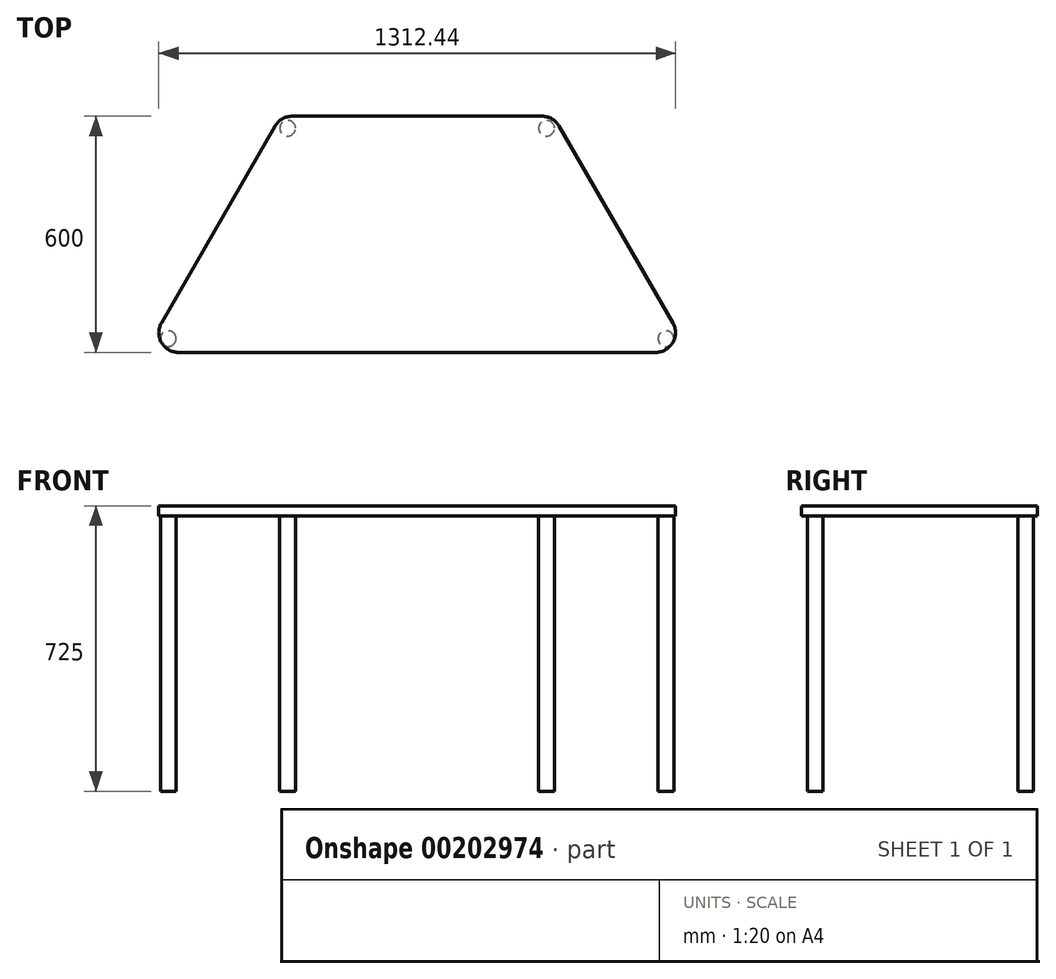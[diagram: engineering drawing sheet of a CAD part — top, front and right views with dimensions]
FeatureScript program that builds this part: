
annotation { "Feature Type Name" : "Feature", "Feature Type Description" : "" }
export const myFeature = defineFeature(function(context is Context, id is Id, definition is map)
    precondition{}
    {
        {
            var Q0;
            Q0=qCreatedBy(makeId("Top.planeOp"),FACE);
            var sketch = newSketch(context, id + "F0", { "sketchPlane" : qUnion([Q0])});
            skLineSegment(sketch, "E0", {"start": v(0, 300) * mm, "end": v(-346.41, 300) * mm});
            skLineSegment(sketch, "E1", {"start": v(-346.41, 300) * mm, "end": v(-692.82, -300) * mm});
            skLineSegment(sketch, "E2", {"start": v(-692.82, -300) * mm, "end": v(0, -300) * mm});
            skLineSegment(sketch, "E3.MirrorCS", {"start": v(0, 300) * mm, "end": v(346.41, 300) * mm});
            skLineSegment(sketch, "E4.MirrorCS", {"start": v(346.41, 300) * mm, "end": v(692.82, -300) * mm});
            skLineSegment(sketch, "E5.MirrorCS", {"start": v(692.82, -300) * mm, "end": v(0, -300) * mm});
            skLineSegment(sketch, "E6", {"start": v(0, 300) * mm, "end": v(0, 0) * mm});
            skLineSegment(sketch, "E7", {"start": v(0, 0) * mm, "end": v(0, -300) * mm});
            skSolve(sketch);
        }
        {
            var Q0;
            Q0=qCreatedBy(makeId("Top.planeOp"),FACE);
            var sketch = newSketch(context, id + "F1", { "sketchPlane" : qUnion([Q0])});
            skLineSegment(sketch, "E8.0", {"start": v(0, 300) * mm, "end": v(-346.41, 300) * mm, "construction": true});
            skLineSegment(sketch, "E9.0", {"start": v(-346.41, 300) * mm, "end": v(-692.82, -300) * mm, "construction": true});
            skLineSegment(sketch, "E10.0", {"start": v(-692.82, -300) * mm, "end": v(0, -300) * mm, "construction": true});
            skLineSegment(sketch, "E11", {"start": v(-346.41, 300) * mm, "end": v(-328.91, 269.69) * mm, "construction": true});
            skCircle(sketch, "E12", {"center": v(-328.91, 269.69) * mm, "radius": 20 * mm});
            skLineSegment(sketch, "E13", {"start": v(-692.82, -300) * mm, "end": v(-632.2, -265) * mm, "construction": true});
            skCircle(sketch, "E14", {"center": v(-632.2, -265) * mm, "radius": 20 * mm});
            skCircle(sketch, "E15.MirrorC", {"center": v(328.91, 269.69) * mm, "radius": 20 * mm});
            skCircle(sketch, "E16.MirrorC", {"center": v(632.2, -265) * mm, "radius": 20 * mm});
            skSolve(sketch);
        }
        {
            var Q0;
            Q0 = qSketchRegion(id + "F0", true);
            extrude(context, id + "F2", {"entities" : qUnion([Q0]), "depth" : 25 * mm});
        }
        {
            var Q0;
            Q0 = qSketchRegion(id + "F1", true);
            extrude(context, id + "F3", {"entities" : qUnion([Q0]), "operationType" : NewBodyOperationType.ADD, "oppositeDirection" : true, "depth" : 700 * mm});
        }
        {
            var Q0;
            Q0=makeQuery(id+"F2.opExtrude","SWEPT_EDGE",EDGE,{"disambiguationData":[OSD([sQuery(id+"F0.wireOp",EDGE,"E1"),sQuery(id+"F0.wireOp",EDGE,"E2")])]});
            var Q1;
            Q1=makeQuery(id+"F2.opExtrude","SWEPT_EDGE",EDGE,{"disambiguationData":[OSD([sQuery(id+"F0.wireOp",EDGE,"E0"),sQuery(id+"F0.wireOp",EDGE,"E1")])]});
            var Q2;
            Q2=makeQuery(id+"F2.opExtrude","SWEPT_EDGE",EDGE,{"disambiguationData":[OSD([sQuery(id+"F0.wireOp",EDGE,"E3.MirrorCS"),sQuery(id+"F0.wireOp",EDGE,"E4.MirrorCS")])]});
            var Q3;
            Q3=makeQuery(id+"F2.opExtrude","SWEPT_EDGE",EDGE,{"disambiguationData":[OSD([sQuery(id+"F0.wireOp",EDGE,"E4.MirrorCS"),sQuery(id+"F0.wireOp",EDGE,"E5.MirrorCS")])]});
            fillet(context, id + "F4", {"entities" : qUnion([Q0, Q1, Q2, Q3]), "radius" : 50 * mm, "tangentPropagation" : true, "allowEdgeOverflow" : false});
        }
    });
